# Revit family: 2
name_source: partatom
category: Pipe Accessories
revit_build: Autodesk Revit 2018 (Build: 20190510_1515(x64)
units: mm (PartAtom-declared; Revit-internal decimal feet)

## family parameters
Always vertical = No
Cut with Voids When Loaded = No
OmniClass Number = 23.65.00.00
OmniClass Title = Supply and Distribution of Liquids and Gases
Part Type = Normal
Round Connector Dimension = Use Diameter
Shared = No
Work Plane-Based = No

## types (1)
- Defauly - please load Revit Family Type Catalog
    1 = Yes
    1/2 = No
    3/4 = No
    Antifreeze: = Passiveted Propylene Glycol
    Application fluids = Water or glycol solutions
    BIMobject category = HVAC:Other HVAC
    Brand url = www.pintossi.it
    C = 0 mm  [stored 0 ft]
    Closing tolerance = 20%
    Coeff. of outflow (K) = 0.87
    Conditioning: = as indicated by the producer
    Copper (CU): = < 0,1 mg/kg (< 0,05 mg/kg for steam)
    Cross section = 4909 cm³
    D = 0 mm  [stored 0 ft]
    Description = Pintossi+C safety relief valve is designed in order to open automatically when the internal pressure of the system exceeds a pre-set maximum pressure value, by discharging the fluid throught it. Once the pressure of the system returns below the pre-set maximum value the safety valve closes automatically. This safety feature prevents reaching dangerous pressure levels which may damage and affect the components installed in the system.

Thanks to the ergonomic handwheel the valve can be manually open anytime, for checking the correct functioning

Pintossi+C safety relief valves are designed in compliance with the essential safety requirements stipulated in the EU Pressure Equipment Directive PED 2014/68/EU (Pressure Equipment Directive) and marked with CE logo. WRAS certified.

Available with manomter gauge art.583
    Design country = Italy
    E = 35 mm
    Edition number = 0
    F = 30 mm  [stored 0.0984252 ft]
    Flow rate of discharge (kg/h) = 860
    Fluid aspect: = Limpid
    G = 74 mm
    Generator Potential (kW) = 500
    Height Connector = 30 mm  [stored 0.0984252 ft]
    IFC Classification = Valve
    Inlet/Outlet Diameter = 25 mm  [stored 0.082021 ft]
    Iron (FE): = < 0,5 mg/kg (< 0,1 mg/kg for steam)
    Main Inlet/Outlet Diameter = 25 mm  [stored 0.082021 ft]
    Manufacturer = pintossi+C
    Manufacturer country = Italy
    Mass = 0.00 kg
    Masterformat 2014 Code = 23 00 00
    Masterformat 2014 Description = Ventilating, and Air contitioning (HVAC)
    Material Body = Pintossi - Metal - Brass CW617N
    Material Gaskets = Pintossi - Rubber - NBR
    Material Polimer = Pintossi - Plastic - Red
    Maximum discharge pressure = 0.0 bar
    Maximum percentage of glycol [%] = 30
    Maximum working pressure = 10.0 bar
    Maximum working temperature = 100 °C
    Model = 581 FEMALE SAFETY VALVE
    NBS Reference Code = 55-34-05
    NBS Reference Description = Automatic Air Vents
    OmniClass Code = 23-27 31 00
    OmniClass Description = Valves
    Opening overpressure = 10%
    PH: = Between 7 and 8
    Pressure of setting = 3.0 bar
    Product Guid = 9d0fdbec-e921-4dcd-9137-0e7e1bdf3134
    Product SKU = 581-FEMALE-SAFETY-VALVE
    Product data url = https://www.bimobject.com
    Product family = COMPONENTS-FOR-CENTRAL-HEATING-SYSTEMS
    Product group = SYSTEMS-SAFETY-VALVES
    QR code = https://www.bimobject.com
    Tolerance = 10% for valves with pre-set pressure <5bar. 0,5 bar for valves with pre-set pressure >5bar
    UNSPSC Code = 401446
    URL = www.pintossi.it
    Uniclass 1.4 Code = JT10
    Uniclass 1.4 Description = Heating systems
    Uniclass 2.0 Code = PR-55-34-05
    Uniclass 2.0 Description = Automatic Air Vents
    Uniclass 2015 Code = Ss_60
    Uniclass 2015 Name = Heating, cooling and refrigeration systems
    Uniformat II Code = D30
    Uniformat II Description = HVAC
    length Connrector = 35 mm

note: [stored X ft] marks values corroborated as IEEE doubles in the binary element streams (Revit-internal decimal feet)

## geometry (parser evidence)
native form markers: Sweep x2
no freeform markers — native parametric forms only
